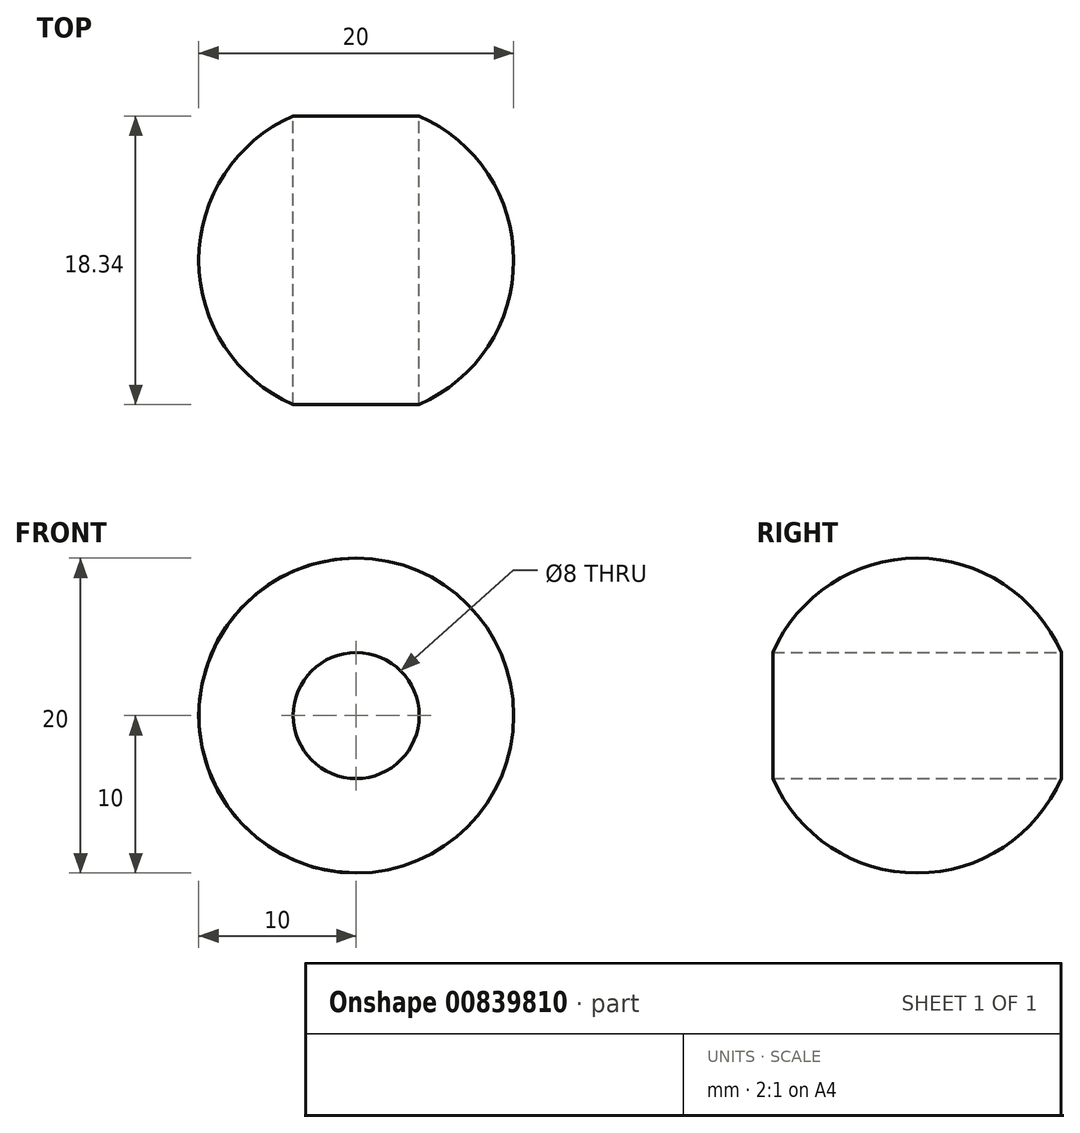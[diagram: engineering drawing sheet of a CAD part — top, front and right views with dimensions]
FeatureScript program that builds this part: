
annotation { "Feature Type Name" : "Feature", "Feature Type Description" : "" }
export const myFeature = defineFeature(function(context is Context, id is Id, definition is map)
    precondition{}
    {
        {
            var Q0;
            Q0=qCreatedBy(makeId("Front.planeOp"),FACE);
            var sketch = newSketch(context, id + "F0", { "sketchPlane" : qUnion([Q0])});
            skArc(sketch, "E0", {"start": v(0, 10) * mm, "mid": v(-10, 0) * mm, "end": v(0, -10) * mm});
            skLineSegment(sketch, "E1", {"start": v(0, 10) * mm, "end": v(0, -10) * mm});
            skSolve(sketch);
        }
        {
            var Q0;
            Q0=makeQuery(id+"F0.imprint","IMPRINT",FACE,{"disambiguationData":[TD([[makeQuery(id+"F0.imprint","IMPRINT",EDGE,{"derivedFrom":sQuery(id+"F0.wireOp",EDGE,"E0")}),1.0]])]});
            var Q1;
            Q1=sQuery(id+"F0.wireOp",EDGE,"E1");
            revolve(context, id + "F1", {"surfaceOperationType" : NewSurfaceOperationType.NEW, "entities" : qUnion([Q0]), "axis" : qUnion([Q1]), "revolveType" : RevolveType.FULL});
        }
        {
            var Q0;
            Q0=qCreatedBy(makeId("Front.planeOp"),FACE);
            var sketch = newSketch(context, id + "F2", { "sketchPlane" : qUnion([Q0])});
            skCircle(sketch, "E2", {"center": v(0, 0) * mm, "radius": 4 * mm});
            skSolve(sketch);
        }
        {
            var Q0;
            Q0 = qSketchRegion(id + "F2", true);
            extrude(context, id + "F3", {"entities" : qUnion([Q0]), "operationType" : NewBodyOperationType.REMOVE, "depth" : 10 * mm, "offsetDistance" : 25 * mm, "hasSecondDirection" : true, "secondDirectionOppositeDirection" : true, "secondDirectionDepth" : 10 * mm});
        }
    });
